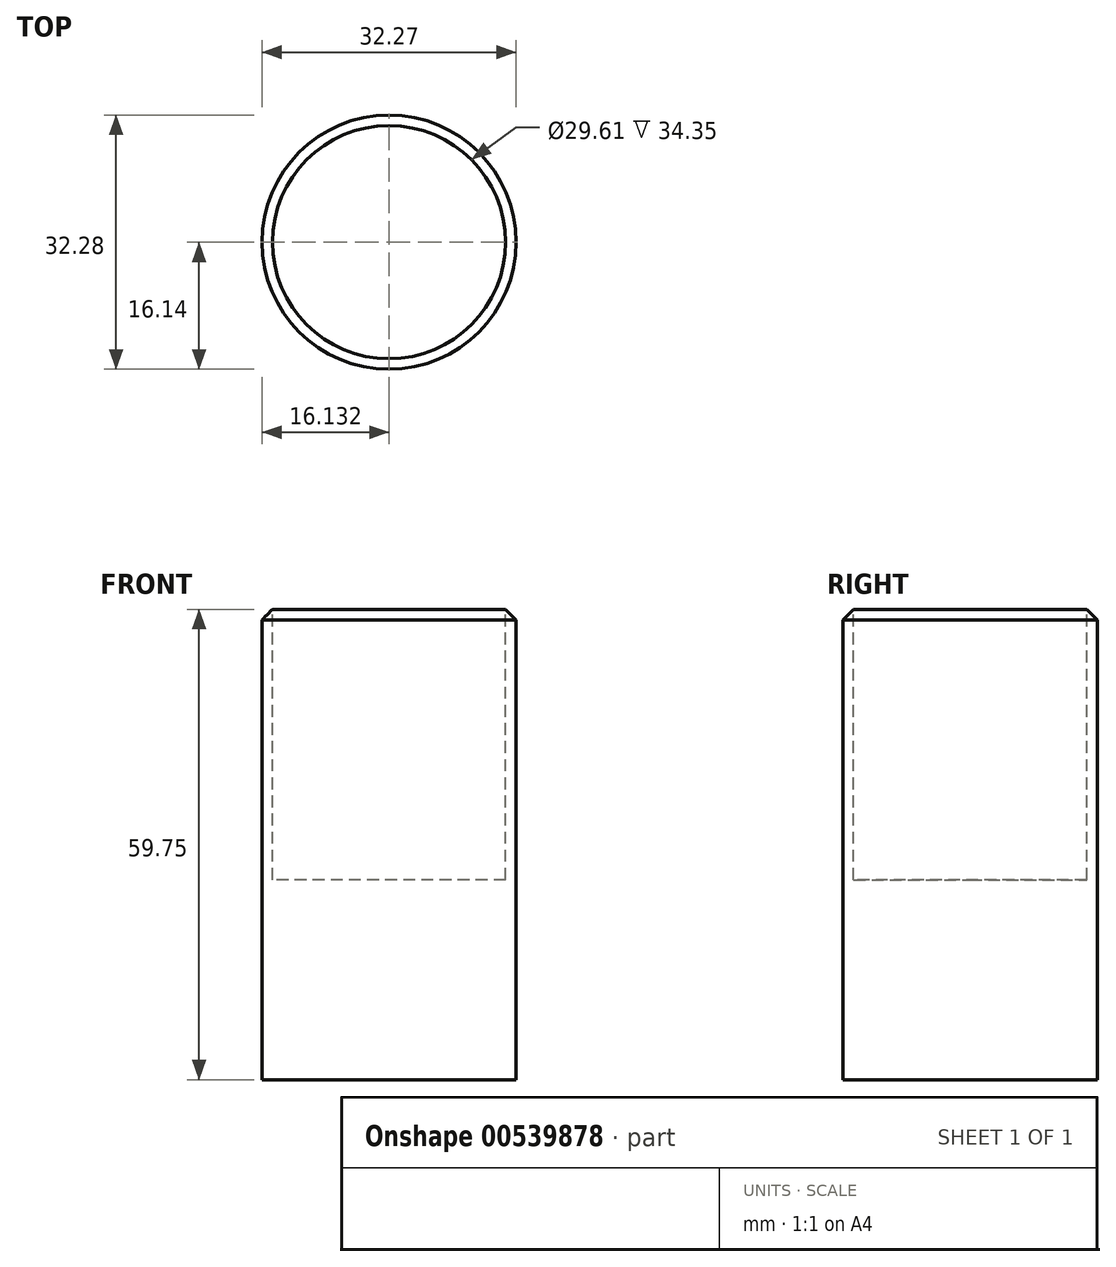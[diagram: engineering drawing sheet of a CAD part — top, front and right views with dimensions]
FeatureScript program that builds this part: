
annotation { "Feature Type Name" : "Feature", "Feature Type Description" : "" }
export const myFeature = defineFeature(function(context is Context, id is Id, definition is map)
    precondition{}
    {
        {
            var Q0;
            Q0=qCreatedBy(makeId("Front.planeOp"),FACE);
            var sketch = newSketch(context, id + "F0", { "sketchPlane" : qUnion([Q0])});
            skLineSegment(sketch, "E0.bottom", {"start": v(-62.02, 60.66) * mm, "end": v(59.04, 60.66) * mm});
            skLineSegment(sketch, "E0.top", {"start": v(-62.02, -57.68) * mm, "end": v(59.04, -57.68) * mm});
            skLineSegment(sketch, "E0.left", {"start": v(-62.02, 60.66) * mm, "end": v(-62.02, -57.68) * mm});
            skLineSegment(sketch, "E0.right", {"start": v(59.04, 60.66) * mm, "end": v(59.04, -57.68) * mm});
            skLineSegment(sketch, "E1", {"start": v(-14.68, 34.29) * mm, "end": v(-14.68, -29.21) * mm});
            skLineSegment(sketch, "E2", {"start": v(-14.68, -29.21) * mm, "end": v(-30.81, -29.21) * mm});
            skLineSegment(sketch, "E3", {"start": v(-30.81, -29.21) * mm, "end": v(-30.81, 34.29) * mm});
            skLineSegment(sketch, "E4", {"start": v(-30.81, 34.29) * mm, "end": v(-14.68, 34.29) * mm});
            skSolve(sketch);
        }
        {
            var Q0;
            Q0=makeQuery(id+"F0.imprint","IMPRINT",FACE,{"disambiguationData":[TD([[makeQuery(id+"F0.imprint","IMPRINT",EDGE,{"derivedFrom":sQuery(id+"F0.wireOp",EDGE,"E1")}),-1.0]])]});
            var Q1;
            Q1=sQuery(id+"F0.wireOp",EDGE,"E1");
            revolve(context, id + "F1", {"entities" : qUnion([Q0]), "axis" : qUnion([Q1]), "revolveType" : RevolveType.FULL});
        }
        {
            var Q0;
            Q0=makeQuery(id+"F1.opRevolve","SWEPT_FACE",FACE,{"disambiguationData":[OSD([sQuery(id+"F0.wireOp",EDGE,"E4")])]});
            var sketch = newSketch(context, id + "F2", { "sketchPlane" : qUnion([Q0])});
            skCircle(sketch, "E5", {"center": v(-14.68, 0) * mm, "radius": 14.8 * mm});
            skSolve(sketch);
        }
        {
            var Q0;
            Q0=makeQuery(id+"F2.imprint","IMPRINT",FACE,{"disambiguationData":[TD([[makeQuery(id+"F2.imprint","IMPRINT",EDGE,{"derivedFrom":sQuery(id+"F2.wireOp",EDGE,"E5")}),1.0]])]});
            extrude(context, id + "F3", {"entities" : qUnion([Q0]), "operationType" : NewBodyOperationType.REMOVE, "oppositeDirection" : true, "depth" : 38.1 * mm, "offsetDistance" : 25.4 * mm});
        }
        {
            var Q0;
            Q0=makeQuery(id+"F1.opRevolve","SWEPT_EDGE",EDGE,{"disambiguationData":[OSD([sQuery(id+"F0.wireOp",EDGE,"E3"),sQuery(id+"F0.wireOp",EDGE,"E4")])]});
            chamfer(context, id + "F4", {"entities" : qUnion([Q0]), "width" : 5.08 * mm, "tangentPropagation" : true});
        }
    });
